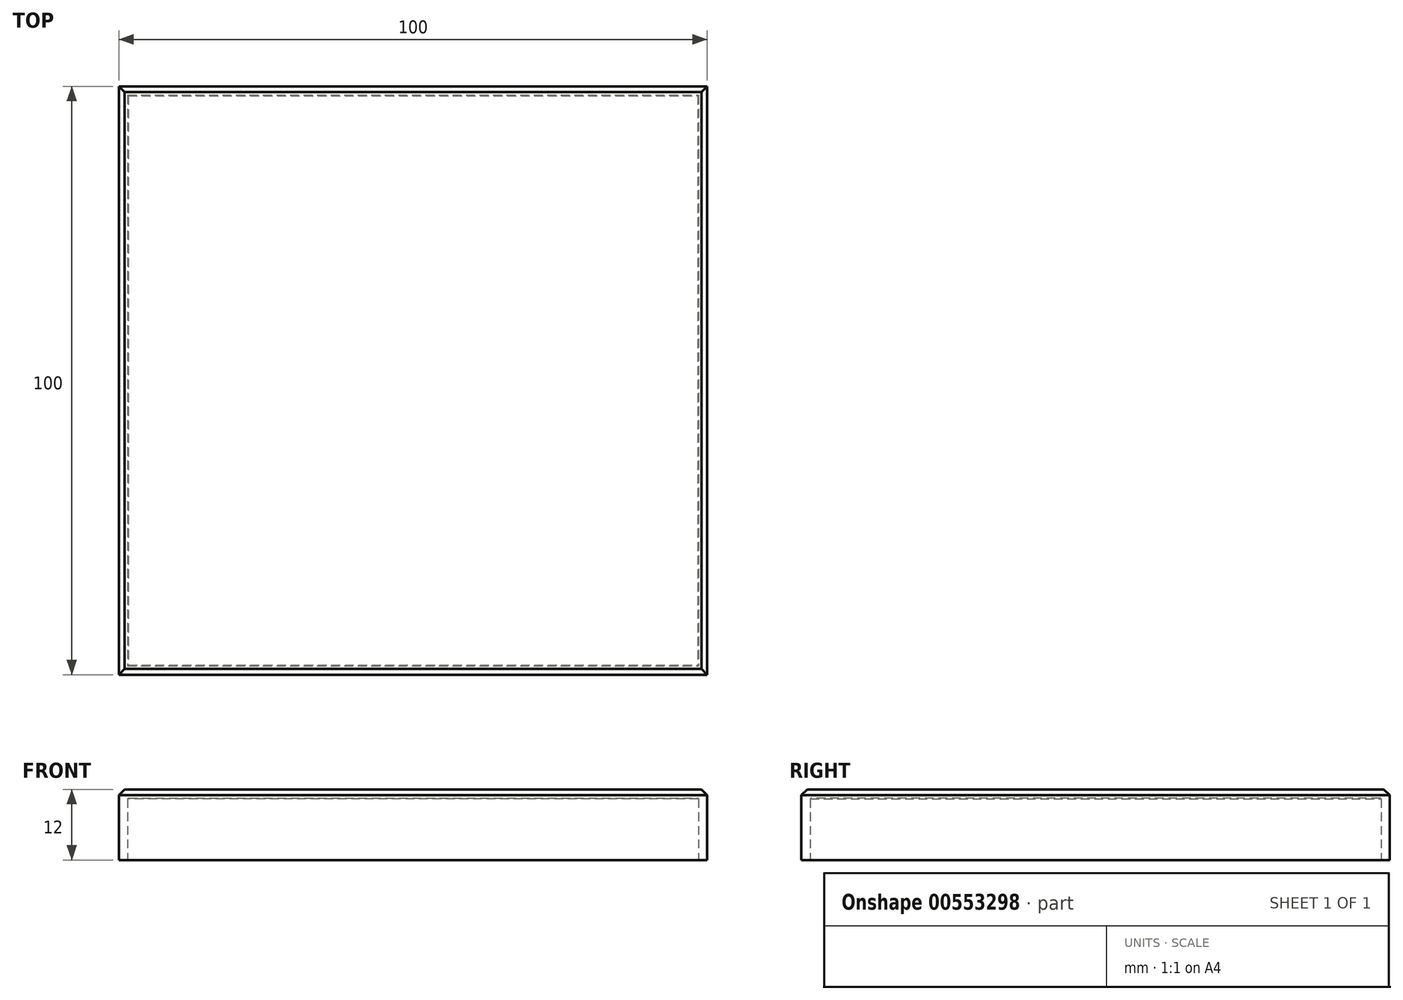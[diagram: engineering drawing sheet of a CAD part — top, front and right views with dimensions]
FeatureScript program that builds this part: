
annotation { "Feature Type Name" : "Feature", "Feature Type Description" : "" }
export const myFeature = defineFeature(function(context is Context, id is Id, definition is map)
    precondition{}
    {
        {
            var Q0;
            Q0=qCreatedBy(makeId("Top.planeOp"),FACE);
            var sketch = newSketch(context, id + "F0", { "sketchPlane" : qUnion([Q0])});
            skLineSegment(sketch, "E0.bottom", {"start": v(0, 0) * mm, "end": v(100, 0) * mm});
            skLineSegment(sketch, "E0.top", {"start": v(0, -100) * mm, "end": v(100, -100) * mm});
            skLineSegment(sketch, "E0.left", {"start": v(0, 0) * mm, "end": v(0, -100) * mm});
            skLineSegment(sketch, "E0.right", {"start": v(100, 0) * mm, "end": v(100, -100) * mm});
            skSolve(sketch);
        }
        {
            var Q0;
            Q0=makeQuery(id+"F0.imprint","IMPRINT",FACE,{"disambiguationData":[TD([[makeQuery(id+"F0.imprint","IMPRINT",EDGE,{"derivedFrom":sQuery(id+"F0.wireOp",EDGE,"E0.bottom")}),-1.0]])]});
            extrude(context, id + "F1", {"entities" : qUnion([Q0]), "depth" : 12 * mm, "offsetDistance" : 25 * mm});
        }
        {
            var Q0;
            Q0=makeQuery(id+"F1.opExtrude","CAP_EDGE",EDGE,{"disambiguationData":[OSD([sQuery(id+"F0.wireOp",EDGE,"E0.left")])],"isStart":false});
            var Q1;
            Q1=makeQuery(id+"F1.opExtrude","CAP_EDGE",EDGE,{"disambiguationData":[OSD([sQuery(id+"F0.wireOp",EDGE,"E0.top")])],"isStart":false});
            var Q2;
            Q2=makeQuery(id+"F1.opExtrude","CAP_EDGE",EDGE,{"disambiguationData":[OSD([sQuery(id+"F0.wireOp",EDGE,"E0.right")])],"isStart":false});
            var Q3;
            Q3=makeQuery(id+"F1.opExtrude","CAP_EDGE",EDGE,{"disambiguationData":[OSD([sQuery(id+"F0.wireOp",EDGE,"E0.bottom")])],"isStart":false});
            chamfer(context, id + "F2", {"entities" : qUnion([Q0, Q1, Q2, Q3]), "width" : 1 * mm, "tangentPropagation" : true});
        }
        {
            var Q0;
            Q0=makeQuery(id+"F1.opExtrude","CAP_FACE",FACE,{"disambiguationData":[OSD([sQuery(id+"F0.wireOp",EDGE,"E0.bottom"),sQuery(id+"F0.wireOp",EDGE,"E0.top"),sQuery(id+"F0.wireOp",EDGE,"E0.left"),sQuery(id+"F0.wireOp",EDGE,"E0.right")])],"isStart":true});
            shell(context, id + "F3", {"entities" : qUnion([Q0]), "thickness" : 1.5 * mm});
        }
    });
